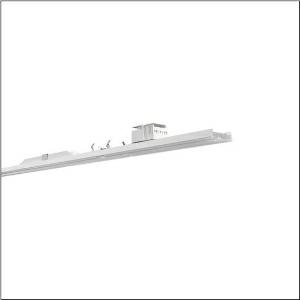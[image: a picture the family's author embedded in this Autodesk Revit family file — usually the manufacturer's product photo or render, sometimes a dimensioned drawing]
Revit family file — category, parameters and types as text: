
# Revit family: licross_r__11_recessed_mo_51tl127n48xf_abf8
name_source: partatom
category: Lighting Fixtures
units: mm (PartAtom-declared; Revit-internal decimal feet)

## family parameters
Cut with Voids When Loaded = No
Host = Face
Light Source = No
Part Type = Normal
Room Calculation Point = No
Round Connector Dimension = Use Diameter
Shared = No

## types (1)
- Licross® 11 Recessed MO (1 x LED, 8350 lm, 47.6 W, 4000K)
    Apparent Load = 48 VA
    CIE Flux Codes = 67 92 99 100 100
    Color Rendering = 80
    Color Temperature = 4000K
    Default Elevation = 1800 mm
    Description = Licross® 11 Recessed MOluminaire insert, length: 1.500mm, width: 66mm, height: 67mm, LED rated luminous flux: 8.350lm, light colour: 840, control gear: ON/OFF, control gear: ECG, with plug, 3-pole, with phase selection, mains connection: 220..240V, AC, 50/60Hz, halogen-free wiring, primary optical cover: cover, of PMMA, light emission: direct distribution, protection rating (complete): IP40, insulation class (complete): insulation class I (protective earthing), certification: CE, ENEC, VDE, protection symbol: D if used in an environment without relevant dust loads with corresponding accessories, permissible ambient temperature for indoor applications: -35..+40°C, reducing of maximum allowable ambient temperature of 5°C with ceiling mounting, corresponds to IFS (International Featured Standards) requirements for safety and quality in the food industry, packaging unit: 1 piece
    Height = 58 mm
    Lamp = 1 x LED
    Lamp Light Flux = 8350 lm
    Lamp Power = 47.6 W
    Lamp count = 1
    Length = 1500 mm
    Luminous efficacy = 175 lm/W
    Manufacturer = Siteco
    ModVariant = No
    Model = 51TL127N48XF
    Mounting Place = Ceiling
    Mounting Type = Pendant
    Number of Poles = 1
    OnlyDefault = Yes
    Power Factor = 1
    Product Name = Licross® 11 Recessed MO
    Product group = luminaire insert
    ProductGroupID = 902
    Protection Class = Protection class I
    Protection Degree = IP 40
    RLX_Detail_Level = 1
    RlxData = <blob elided: 18665 chars, md5=458b38ab>
    Socket = socket
    Standby Power = 0 W
    System Light Flux = 8350 lm
    System Power = 48 W
    Type Comments = Product without accessories
    Type Image = l_1266722.jpg
    URL = http://relux.com
    VarID = ---
    Voltage = 0 V
    Weight = 0.00 kg
    Width = 66 mm

## geometry (parser evidence)
native form markers: Blend x4, Sweep x11
no freeform markers — native parametric forms only
